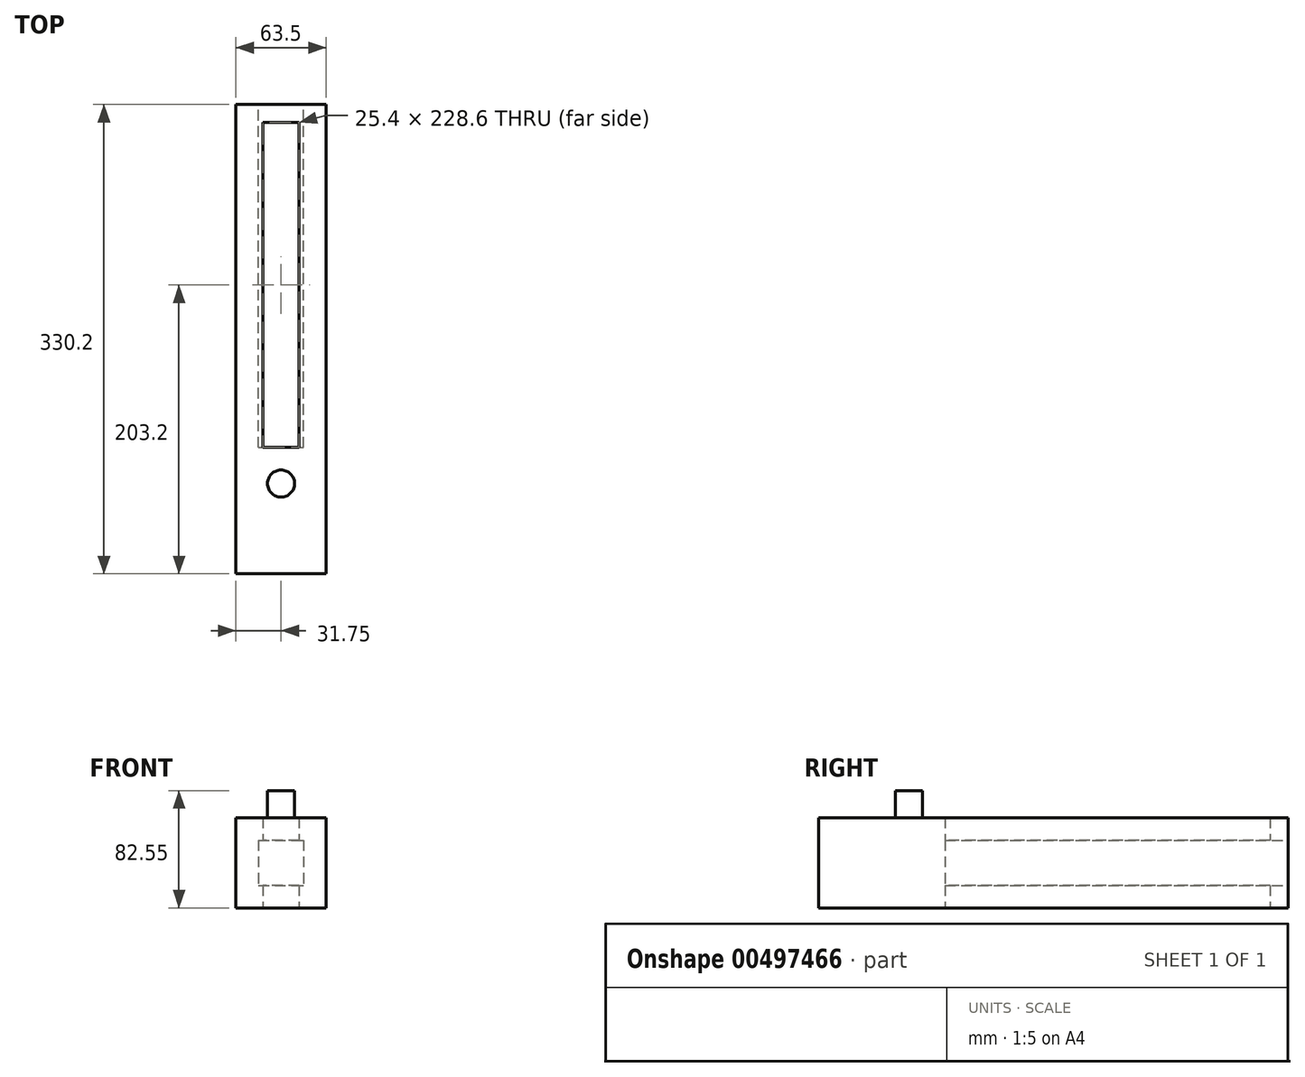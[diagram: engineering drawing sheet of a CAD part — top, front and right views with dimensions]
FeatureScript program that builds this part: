
annotation { "Feature Type Name" : "Feature", "Feature Type Description" : "" }
export const myFeature = defineFeature(function(context is Context, id is Id, definition is map)
    precondition{}
    {
        {
            var Q0;
            Q0=qCreatedBy(makeId("Top.planeOp"),FACE);
            var sketch = newSketch(context, id + "F0", { "sketchPlane" : qUnion([Q0])});
            skLineSegment(sketch, "E0.bottom", {"start": v(31.75, 165.1) * mm, "end": v(-31.75, 165.1) * mm});
            skLineSegment(sketch, "E0.top", {"start": v(31.75, -165.1) * mm, "end": v(-31.75, -165.1) * mm});
            skLineSegment(sketch, "E0.left", {"start": v(31.75, 165.1) * mm, "end": v(31.75, -165.1) * mm});
            skLineSegment(sketch, "E0.right", {"start": v(-31.75, 165.1) * mm, "end": v(-31.75, -165.1) * mm});
            skPoint(sketch, "E0.middle", {"position": v(0, 0) * mm});
            skLineSegment(sketch, "E1.bottom", {"start": v(12.7, 152.4) * mm, "end": v(-12.7, 152.4) * mm});
            skLineSegment(sketch, "E1.top", {"start": v(12.7, -76.2) * mm, "end": v(-12.7, -76.2) * mm});
            skLineSegment(sketch, "E1.left", {"start": v(12.7, 152.4) * mm, "end": v(12.7, -76.2) * mm});
            skLineSegment(sketch, "E1.right", {"start": v(-12.7, 152.4) * mm, "end": v(-12.7, -76.2) * mm});
            skPoint(sketch, "E1.middle", {"position": v(0, 38.1) * mm});
            skSolve(sketch);
        }
        {
            var Q0;
            Q0=makeQuery(id+"F0.imprint","IMPRINT",FACE,{"disambiguationData":[TD([[makeQuery(id+"F0.imprint","IMPRINT",EDGE,{"derivedFrom":sQuery(id+"F0.wireOp",EDGE,"E0.bottom")}),1.0]])]});
            extrude(context, id + "F1", {"entities" : qUnion([Q0]), "endBound" : BoundingType.SYMMETRIC, "depth" : 63.5 * mm});
        }
        {
            var Q0;
            Q0=makeQuery(id+"F1.opExtrude","SWEPT_FACE",FACE,{"disambiguationData":[OSD([sQuery(id+"F0.wireOp",EDGE,"E0.bottom")])]});
            var sketch = newSketch(context, id + "F2", { "sketchPlane" : qUnion([Q0])});
            skLineSegment(sketch, "E2.bottom", {"start": v(15.87, 15.88) * mm, "end": v(-15.88, 15.88) * mm});
            skLineSegment(sketch, "E2.top", {"start": v(15.88, -15.88) * mm, "end": v(-15.87, -15.88) * mm});
            skLineSegment(sketch, "E2.left", {"start": v(15.87, 15.88) * mm, "end": v(15.88, -15.88) * mm});
            skLineSegment(sketch, "E2.right", {"start": v(-15.88, 15.88) * mm, "end": v(-15.87, -15.88) * mm});
            skPoint(sketch, "E2.middle", {"position": v(0, 0) * mm});
            skSolve(sketch);
        }
        {
            var Q0;
            Q0=makeQuery(id+"F2.imprint","IMPRINT",FACE,{"disambiguationData":[TD([[makeQuery(id+"F2.imprint","IMPRINT",EDGE,{"derivedFrom":sQuery(id+"F2.wireOp",EDGE,"E2.bottom")}),1.0]])]});
            extrude(context, id + "F3", {"entities" : qUnion([Q0]), "operationType" : NewBodyOperationType.REMOVE, "oppositeDirection" : true, "depth" : 241.3 * mm});
        }
        {
            var Q0;
            Q0=makeQuery(id+"F1.opExtrude","CAP_FACE",FACE,{"disambiguationData":[OSD([sQuery(id+"F0.wireOp",EDGE,"E0.bottom"),sQuery(id+"F0.wireOp",EDGE,"E0.top"),sQuery(id+"F0.wireOp",EDGE,"E0.left"),sQuery(id+"F0.wireOp",EDGE,"E0.right"),sQuery(id+"F0.wireOp",EDGE,"E1.bottom"),sQuery(id+"F0.wireOp",EDGE,"E1.top"),sQuery(id+"F0.wireOp",EDGE,"E1.left"),sQuery(id+"F0.wireOp",EDGE,"E1.right")])],"isStart":false});
            var sketch = newSketch(context, id + "F4", { "sketchPlane" : qUnion([Q0])});
            skCircle(sketch, "E3", {"center": v(0, -101.6) * mm, "radius": 9.53 * mm});
            skSolve(sketch);
        }
        {
            var Q0;
            Q0=makeQuery(id+"F4.imprint","IMPRINT",FACE,{"disambiguationData":[TD([[makeQuery(id+"F4.imprint","IMPRINT",EDGE,{"derivedFrom":sQuery(id+"F4.wireOp",EDGE,"E3")}),1.0]])]});
            extrude(context, id + "F5", {"entities" : qUnion([Q0]), "operationType" : NewBodyOperationType.ADD, "depth" : 19.05 * mm});
        }
    });
